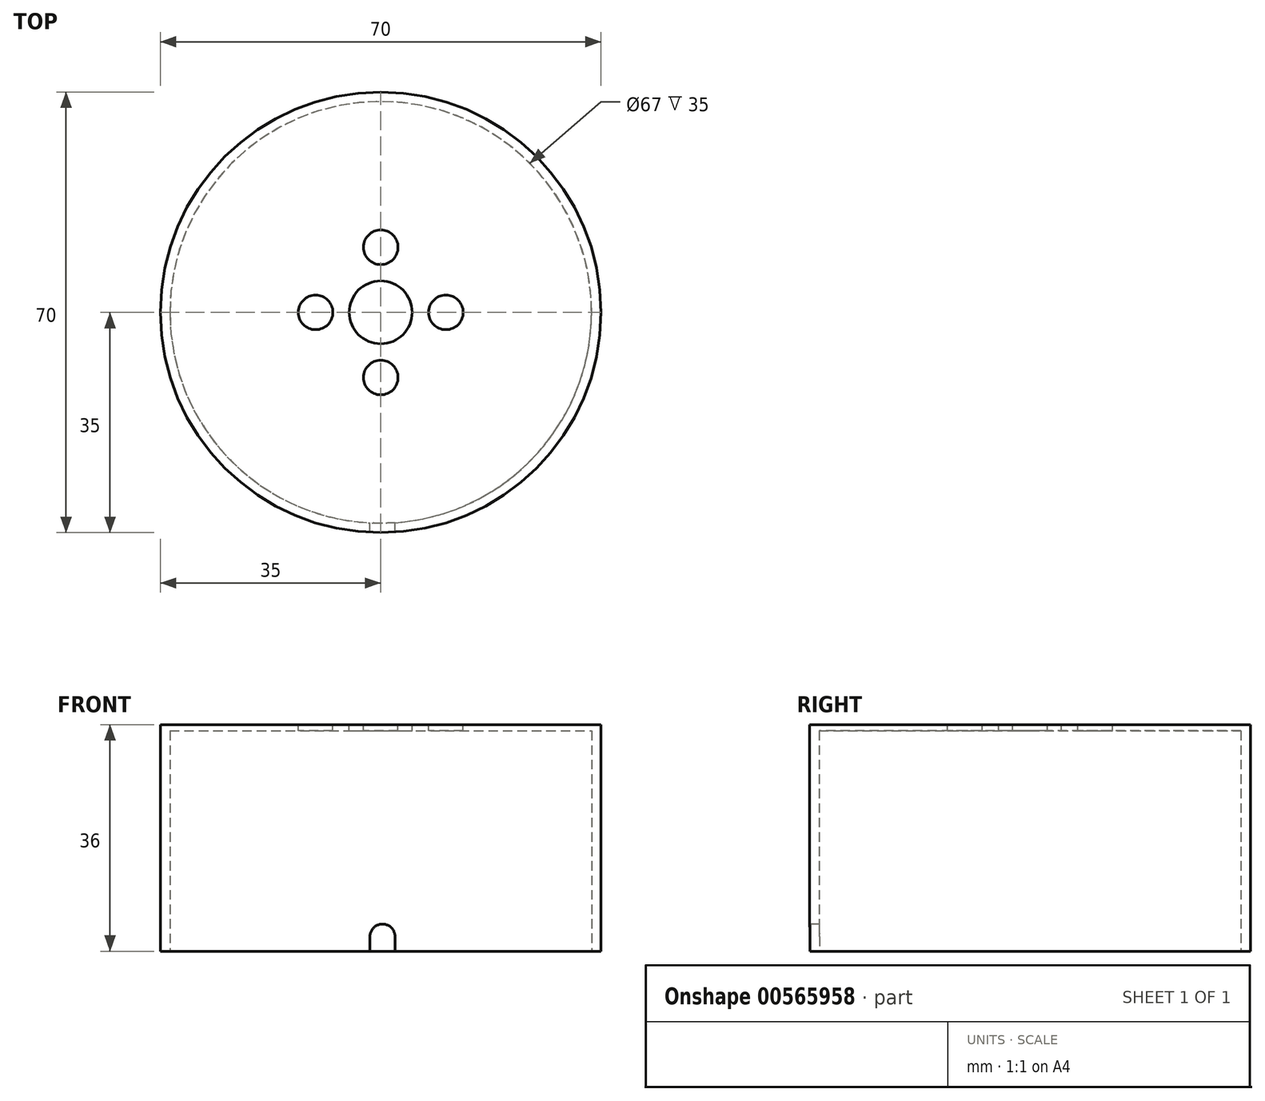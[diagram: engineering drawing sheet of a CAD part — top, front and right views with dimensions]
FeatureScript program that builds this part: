
annotation { "Feature Type Name" : "Feature", "Feature Type Description" : "" }
export const myFeature = defineFeature(function(context is Context, id is Id, definition is map)
    precondition{}
    {
        {
            var Q0;
            Q0=qCreatedBy(makeId("Top.planeOp"),FACE);
            var sketch = newSketch(context, id + "F0", { "sketchPlane" : qUnion([Q0])});
            skCircle(sketch, "E0", {"center": v(0, 0) * mm, "radius": 5 * mm});
            skCircle(sketch, "E1", {"center": v(0, 0) * mm, "radius": 5.5 * mm});
            skLineSegment(sketch, "E2", {"start": v(-0.75, 5.45) * mm, "end": v(-0.75, 25.45) * mm});
            skLineSegment(sketch, "E3", {"start": v(0.75, 5.45) * mm, "end": v(0.75, 25.45) * mm});
            skLineSegment(sketch, "E4", {"start": v(-0.75, 10.35) * mm, "end": v(0.75, 10.35) * mm, "construction": true});
            skCircle(sketch, "E5", {"center": v(0, 10.35) * mm, "radius": 2.75 * mm});
            skLineSegment(sketch, "E6", {"start": v(-0.75, 25.45) * mm, "end": v(0.75, 25.45) * mm});
            skCircle(sketch, "E7.MirrorC", {"center": v(-10.35, 0) * mm, "radius": 2.75 * mm});
            skLineSegment(sketch, "E8.MirrorCS", {"start": v(-5.45, 0.75) * mm, "end": v(-25.45, 0.75) * mm});
            skLineSegment(sketch, "E9.MirrorCS", {"start": v(-5.45, -0.75) * mm, "end": v(-25.45, -0.75) * mm});
            skLineSegment(sketch, "E10.MirrorCS", {"start": v(-25.45, 0.75) * mm, "end": v(-25.45, -0.75) * mm});
            skLineSegment(sketch, "E11.MirrorCS", {"start": v(-0.75, -5.45) * mm, "end": v(-0.75, -25.45) * mm});
            skLineSegment(sketch, "E12.MirrorCS", {"start": v(0.75, -25.45) * mm, "end": v(-0.75, -25.45) * mm});
            skLineSegment(sketch, "E13.MirrorCS", {"start": v(0.75, -5.45) * mm, "end": v(0.75, -25.45) * mm});
            skCircle(sketch, "E14.MirrorC", {"center": v(0, -10.35) * mm, "radius": 2.75 * mm});
            skLineSegment(sketch, "E15.MirrorCS", {"start": v(5.45, -0.75) * mm, "end": v(25.45, -0.75) * mm});
            skLineSegment(sketch, "E16.MirrorCS", {"start": v(25.45, 0.75) * mm, "end": v(25.45, -0.75) * mm});
            skLineSegment(sketch, "E17.MirrorCS", {"start": v(5.45, 0.75) * mm, "end": v(25.45, 0.75) * mm});
            skCircle(sketch, "E18.MirrorC", {"center": v(10.35, 0) * mm, "radius": 2.75 * mm});
            skCircle(sketch, "E19", {"center": v(0, 0) * mm, "radius": 35 * mm});
            skSolve(sketch);
        }
        {
            var Q0;
            Q0 = qSketchRegion(id + "F0", true);
            var Q1;
            {var subQ16=sQuery(id+"F0.wireOp",EDGE,"E6");Q1=makeQuery(id+"F0.imprint","IMPRINT",FACE,{"disambiguationData":[TD([[makeQuery(id+"F0.imprint","IMPRINT",EDGE,{"derivedFrom":subQ16}),1.0]])]});}
            var Q2;
            {var subQ0=sQuery(id+"F0.wireOp",EDGE,"E14.MirrorC");var subQ1=sQuery(id+"F0.wireOp",EDGE,"E11.MirrorCS");var subQ2=makeQuery(id+"F0.imprint","INTERSECT",VERTEX,{"disambiguationData":[OD(0.0)],"derivedFrom":[subQ1,subQ0]});Q2=makeQuery(id+"F0.imprint","IMPRINT",FACE,{"disambiguationData":[TD([[makeQuery(id+"F0.imprint","IMPRINT",EDGE,{"disambiguationData":[TD([[subQ2,-1.0]])],"derivedFrom":subQ1}),1.0]])]});}
            var Q3;
            {var subQ0=sQuery(id+"F0.wireOp",EDGE,"E18.MirrorC");var subQ1=sQuery(id+"F0.wireOp",EDGE,"E15.MirrorCS");var subQ2=makeQuery(id+"F0.imprint","INTERSECT",VERTEX,{"disambiguationData":[OD(0.0)],"derivedFrom":[subQ1,subQ0]});Q3=makeQuery(id+"F0.imprint","IMPRINT",FACE,{"disambiguationData":[TD([[makeQuery(id+"F0.imprint","IMPRINT",EDGE,{"disambiguationData":[TD([[subQ2,-1.0]])],"derivedFrom":subQ1}),1.0]])]});}
            var Q4;
            {var subQ0=sQuery(id+"F0.wireOp",EDGE,"E8.MirrorCS");var subQ1=sQuery(id+"F0.wireOp",EDGE,"E1");var subQ2=makeQuery(id+"F0.imprint","INTERSECT",VERTEX,{"derivedFrom":[subQ1,subQ0]});Q4=makeQuery(id+"F0.imprint","IMPRINT",FACE,{"disambiguationData":[TD([[makeQuery(id+"F0.imprint","IMPRINT",EDGE,{"disambiguationData":[TD([[subQ2,-1.0]])],"derivedFrom":subQ1}),-1.0]])]});}
            var Q5;
            {var subQ0=sQuery(id+"F0.wireOp",EDGE,"E8.MirrorCS");var subQ1=sQuery(id+"F0.wireOp",EDGE,"E7.MirrorC");var subQ2=makeQuery(id+"F0.imprint","INTERSECT",VERTEX,{"disambiguationData":[OD(0.0)],"derivedFrom":[subQ1,subQ0]});Q5=makeQuery(id+"F0.imprint","IMPRINT",FACE,{"disambiguationData":[TD([[makeQuery(id+"F0.imprint","IMPRINT",EDGE,{"disambiguationData":[TD([[subQ2,-1.0]])],"derivedFrom":subQ1}),-1.0]])]});}
            var Q6;
            {var subQ0=sQuery(id+"F0.wireOp",EDGE,"E6");Q6=makeQuery(id+"F0.imprint","IMPRINT",FACE,{"disambiguationData":[TD([[makeQuery(id+"F0.imprint","IMPRINT",EDGE,{"derivedFrom":subQ0}),-1.0]])]});}
            var Q7;
            {var subQ0=sQuery(id+"F0.wireOp",EDGE,"E9.MirrorCS");var subQ1=sQuery(id+"F0.wireOp",EDGE,"E7.MirrorC");var subQ2=makeQuery(id+"F0.imprint","INTERSECT",VERTEX,{"disambiguationData":[OD(0.0)],"derivedFrom":[subQ1,subQ0]});Q7=makeQuery(id+"F0.imprint","IMPRINT",FACE,{"disambiguationData":[TD([[makeQuery(id+"F0.imprint","IMPRINT",EDGE,{"disambiguationData":[TD([[subQ2,-1.0]])],"derivedFrom":subQ1}),-1.0]])]});}
            var Q8;
            {var subQ5=sQuery(id+"F0.wireOp",EDGE,"E10.MirrorCS");Q8=makeQuery(id+"F0.imprint","IMPRINT",FACE,{"disambiguationData":[TD([[makeQuery(id+"F0.imprint","IMPRINT",EDGE,{"derivedFrom":subQ5}),1.0]])]});}
            var Q9;
            {var subQ0=sQuery(id+"F0.wireOp",EDGE,"E14.MirrorC");var subQ1=sQuery(id+"F0.wireOp",EDGE,"E11.MirrorCS");var subQ2=makeQuery(id+"F0.imprint","INTERSECT",VERTEX,{"disambiguationData":[OD(0.0)],"derivedFrom":[subQ1,subQ0]});Q9=makeQuery(id+"F0.imprint","IMPRINT",FACE,{"disambiguationData":[TD([[makeQuery(id+"F0.imprint","IMPRINT",EDGE,{"disambiguationData":[TD([[subQ2,-1.0]])],"derivedFrom":subQ1}),-1.0]])]});}
            var Q10;
            {var subQ0=sQuery(id+"F0.wireOp",EDGE,"E12.MirrorCS");Q10=makeQuery(id+"F0.imprint","IMPRINT",FACE,{"disambiguationData":[TD([[makeQuery(id+"F0.imprint","IMPRINT",EDGE,{"derivedFrom":subQ0}),-1.0]])]});}
            var Q11;
            {var subQ0=sQuery(id+"F0.wireOp",EDGE,"E14.MirrorC");var subQ1=sQuery(id+"F0.wireOp",EDGE,"E13.MirrorCS");var subQ2=makeQuery(id+"F0.imprint","INTERSECT",VERTEX,{"disambiguationData":[OD(0.0)],"derivedFrom":[subQ1,subQ0]});Q11=makeQuery(id+"F0.imprint","IMPRINT",FACE,{"disambiguationData":[TD([[makeQuery(id+"F0.imprint","IMPRINT",EDGE,{"disambiguationData":[TD([[subQ2,-1.0]])],"derivedFrom":subQ1}),1.0]])]});}
            var Q12;
            {var subQ0=sQuery(id+"F0.wireOp",EDGE,"E18.MirrorC");var subQ1=sQuery(id+"F0.wireOp",EDGE,"E15.MirrorCS");var subQ2=makeQuery(id+"F0.imprint","INTERSECT",VERTEX,{"disambiguationData":[OD(0.0)],"derivedFrom":[subQ1,subQ0]});Q12=makeQuery(id+"F0.imprint","IMPRINT",FACE,{"disambiguationData":[TD([[makeQuery(id+"F0.imprint","IMPRINT",EDGE,{"disambiguationData":[TD([[subQ2,-1.0]])],"derivedFrom":subQ1}),-1.0]])]});}
            var Q13;
            {var subQ0=sQuery(id+"F0.wireOp",EDGE,"E16.MirrorCS");Q13=makeQuery(id+"F0.imprint","IMPRINT",FACE,{"disambiguationData":[TD([[makeQuery(id+"F0.imprint","IMPRINT",EDGE,{"derivedFrom":subQ0}),-1.0]])]});}
            var Q14;
            Q14=makeQuery(id+"F0.imprint","IMPRINT",FACE,{"disambiguationData":[TD([[makeQuery(id+"F0.imprint","IMPRINT",EDGE,{"derivedFrom":sQuery(id+"F0.wireOp",EDGE,"E0")}),-1.0]])]});
            var Q15;
            {var subQ0=sQuery(id+"F0.wireOp",EDGE,"E18.MirrorC");var subQ1=sQuery(id+"F0.wireOp",EDGE,"E17.MirrorCS");var subQ2=makeQuery(id+"F0.imprint","INTERSECT",VERTEX,{"disambiguationData":[OD(0.0)],"derivedFrom":[subQ1,subQ0]});Q15=makeQuery(id+"F0.imprint","IMPRINT",FACE,{"disambiguationData":[TD([[makeQuery(id+"F0.imprint","IMPRINT",EDGE,{"disambiguationData":[TD([[subQ2,-1.0]])],"derivedFrom":subQ1}),1.0]])]});}
            var Q16;
            {var subQ0=sQuery(id+"F0.wireOp",EDGE,"E5");var subQ1=sQuery(id+"F0.wireOp",EDGE,"E2");var subQ2=makeQuery(id+"F0.imprint","INTERSECT",VERTEX,{"disambiguationData":[OD(0.0)],"derivedFrom":[subQ1,subQ0]});Q16=makeQuery(id+"F0.imprint","IMPRINT",FACE,{"disambiguationData":[TD([[makeQuery(id+"F0.imprint","IMPRINT",EDGE,{"disambiguationData":[TD([[subQ2,-1.0]])],"derivedFrom":subQ1}),-1.0]])]});}
            var Q17;
            {var subQ0=sQuery(id+"F0.wireOp",EDGE,"E15.MirrorCS");var subQ1=sQuery(id+"F0.wireOp",EDGE,"E1");var subQ2=makeQuery(id+"F0.imprint","INTERSECT",VERTEX,{"derivedFrom":[subQ1,subQ0]});Q17=makeQuery(id+"F0.imprint","IMPRINT",FACE,{"disambiguationData":[TD([[makeQuery(id+"F0.imprint","IMPRINT",EDGE,{"disambiguationData":[TD([[subQ2,-1.0]])],"derivedFrom":subQ1}),-1.0]])]});}
            var Q18;
            {var subQ0=sQuery(id+"F0.wireOp",EDGE,"E11.MirrorCS");var subQ1=sQuery(id+"F0.wireOp",EDGE,"E1");var subQ2=makeQuery(id+"F0.imprint","INTERSECT",VERTEX,{"derivedFrom":[subQ1,subQ0]});Q18=makeQuery(id+"F0.imprint","IMPRINT",FACE,{"disambiguationData":[TD([[makeQuery(id+"F0.imprint","IMPRINT",EDGE,{"disambiguationData":[TD([[subQ2,-1.0]])],"derivedFrom":subQ1}),-1.0]])]});}
            var Q19;
            {var subQ0=sQuery(id+"F0.wireOp",EDGE,"E2");var subQ1=sQuery(id+"F0.wireOp",EDGE,"E1");var subQ2=makeQuery(id+"F0.imprint","INTERSECT",VERTEX,{"derivedFrom":[subQ1,subQ0]});Q19=makeQuery(id+"F0.imprint","IMPRINT",FACE,{"disambiguationData":[TD([[makeQuery(id+"F0.imprint","IMPRINT",EDGE,{"disambiguationData":[TD([[subQ2,1.0]])],"derivedFrom":subQ1}),-1.0]])]});}
            var Q20;
            Q20=makeQuery(id+"F0.imprint","IMPRINT",FACE,{"disambiguationData":[TD([[makeQuery(id+"F0.imprint","IMPRINT",EDGE,{"derivedFrom":sQuery(id+"F0.wireOp",EDGE,"E0")}),1.0]])]});
            var Q21;
            {var subQ0=sQuery(id+"F0.wireOp",EDGE,"E5");var subQ1=sQuery(id+"F0.wireOp",EDGE,"E2");var subQ2=makeQuery(id+"F0.imprint","INTERSECT",VERTEX,{"disambiguationData":[OD(0.0)],"derivedFrom":[subQ1,subQ0]});Q21=makeQuery(id+"F0.imprint","IMPRINT",FACE,{"disambiguationData":[TD([[makeQuery(id+"F0.imprint","IMPRINT",EDGE,{"disambiguationData":[TD([[subQ2,-1.0]])],"derivedFrom":subQ1}),1.0]])]});}
            var Q22;
            {var subQ0=sQuery(id+"F0.wireOp",EDGE,"E5");var subQ1=sQuery(id+"F0.wireOp",EDGE,"E3");var subQ2=makeQuery(id+"F0.imprint","INTERSECT",VERTEX,{"disambiguationData":[OD(0.0)],"derivedFrom":[subQ1,subQ0]});Q22=makeQuery(id+"F0.imprint","IMPRINT",FACE,{"disambiguationData":[TD([[makeQuery(id+"F0.imprint","IMPRINT",EDGE,{"disambiguationData":[TD([[subQ2,-1.0]])],"derivedFrom":subQ1}),-1.0]])]});}
            var Q23;
            {var subQ0=sQuery(id+"F0.wireOp",EDGE,"E8.MirrorCS");var subQ1=sQuery(id+"F0.wireOp",EDGE,"E7.MirrorC");var subQ2=makeQuery(id+"F0.imprint","INTERSECT",VERTEX,{"disambiguationData":[OD(0.0)],"derivedFrom":[subQ1,subQ0]});Q23=makeQuery(id+"F0.imprint","IMPRINT",FACE,{"disambiguationData":[TD([[makeQuery(id+"F0.imprint","IMPRINT",EDGE,{"disambiguationData":[TD([[subQ2,1.0]])],"derivedFrom":subQ1}),-1.0]])]});}
            extrude(context, id + "F1", {"entities" : qUnion([Q0, Q1, Q2, Q3, Q4, Q5, Q6, Q7, Q8, Q9, Q10, Q11, Q12, Q13, Q14, Q15, Q16, Q17, Q18, Q19, Q20, Q21, Q22, Q23]), "oppositeDirection" : true, "depth" : 38 * mm, "offsetDistance" : 25 * mm});
        }
        {
            var Q0;
            {var subQ0=sQuery(id+"F0.wireOp",EDGE,"E9.MirrorCS");var subQ1=sQuery(id+"F0.wireOp",EDGE,"E7.MirrorC");var subQ2=makeQuery(id+"F0.imprint","INTERSECT",VERTEX,{"disambiguationData":[OD(0.0)],"derivedFrom":[subQ1,subQ0]});Q0=makeQuery(id+"F0.imprint","IMPRINT",FACE,{"disambiguationData":[TD([[makeQuery(id+"F0.imprint","IMPRINT",EDGE,{"disambiguationData":[TD([[subQ2,-1.0]])],"derivedFrom":subQ1}),-1.0]])]});}
            var Q1;
            {var subQ0=sQuery(id+"F0.wireOp",EDGE,"E8.MirrorCS");var subQ1=sQuery(id+"F0.wireOp",EDGE,"E7.MirrorC");var subQ2=makeQuery(id+"F0.imprint","INTERSECT",VERTEX,{"disambiguationData":[OD(0.0)],"derivedFrom":[subQ1,subQ0]});Q1=makeQuery(id+"F0.imprint","IMPRINT",FACE,{"disambiguationData":[TD([[makeQuery(id+"F0.imprint","IMPRINT",EDGE,{"disambiguationData":[TD([[subQ2,-1.0]])],"derivedFrom":subQ1}),-1.0]])]});}
            var Q2;
            {var subQ0=sQuery(id+"F0.wireOp",EDGE,"E8.MirrorCS");var subQ1=sQuery(id+"F0.wireOp",EDGE,"E7.MirrorC");var subQ2=makeQuery(id+"F0.imprint","INTERSECT",VERTEX,{"disambiguationData":[OD(0.0)],"derivedFrom":[subQ1,subQ0]});Q2=makeQuery(id+"F0.imprint","IMPRINT",FACE,{"disambiguationData":[TD([[makeQuery(id+"F0.imprint","IMPRINT",EDGE,{"disambiguationData":[TD([[subQ2,1.0]])],"derivedFrom":subQ1}),-1.0]])]});}
            var Q3;
            {var subQ5=sQuery(id+"F0.wireOp",EDGE,"E10.MirrorCS");Q3=makeQuery(id+"F0.imprint","IMPRINT",FACE,{"disambiguationData":[TD([[makeQuery(id+"F0.imprint","IMPRINT",EDGE,{"derivedFrom":subQ5}),1.0]])]});}
            var Q4;
            {var subQ0=sQuery(id+"F0.wireOp",EDGE,"E8.MirrorCS");var subQ1=sQuery(id+"F0.wireOp",EDGE,"E1");var subQ2=makeQuery(id+"F0.imprint","INTERSECT",VERTEX,{"derivedFrom":[subQ1,subQ0]});Q4=makeQuery(id+"F0.imprint","IMPRINT",FACE,{"disambiguationData":[TD([[makeQuery(id+"F0.imprint","IMPRINT",EDGE,{"disambiguationData":[TD([[subQ2,-1.0]])],"derivedFrom":subQ1}),-1.0]])]});}
            var Q5;
            Q5=makeQuery(id+"F0.imprint","IMPRINT",FACE,{"disambiguationData":[TD([[makeQuery(id+"F0.imprint","IMPRINT",EDGE,{"derivedFrom":sQuery(id+"F0.wireOp",EDGE,"E0")}),-1.0]])]});
            var Q6;
            {var subQ0=sQuery(id+"F0.wireOp",EDGE,"E5");var subQ1=sQuery(id+"F0.wireOp",EDGE,"E3");var subQ2=makeQuery(id+"F0.imprint","INTERSECT",VERTEX,{"disambiguationData":[OD(0.0)],"derivedFrom":[subQ1,subQ0]});Q6=makeQuery(id+"F0.imprint","IMPRINT",FACE,{"disambiguationData":[TD([[makeQuery(id+"F0.imprint","IMPRINT",EDGE,{"disambiguationData":[TD([[subQ2,-1.0]])],"derivedFrom":subQ1}),-1.0]])]});}
            var Q7;
            {var subQ0=sQuery(id+"F0.wireOp",EDGE,"E5");var subQ1=sQuery(id+"F0.wireOp",EDGE,"E2");var subQ2=makeQuery(id+"F0.imprint","INTERSECT",VERTEX,{"disambiguationData":[OD(0.0)],"derivedFrom":[subQ1,subQ0]});Q7=makeQuery(id+"F0.imprint","IMPRINT",FACE,{"disambiguationData":[TD([[makeQuery(id+"F0.imprint","IMPRINT",EDGE,{"disambiguationData":[TD([[subQ2,-1.0]])],"derivedFrom":subQ1}),1.0]])]});}
            var Q8;
            {var subQ0=sQuery(id+"F0.wireOp",EDGE,"E5");var subQ1=sQuery(id+"F0.wireOp",EDGE,"E2");var subQ2=makeQuery(id+"F0.imprint","INTERSECT",VERTEX,{"disambiguationData":[OD(0.0)],"derivedFrom":[subQ1,subQ0]});Q8=makeQuery(id+"F0.imprint","IMPRINT",FACE,{"disambiguationData":[TD([[makeQuery(id+"F0.imprint","IMPRINT",EDGE,{"disambiguationData":[TD([[subQ2,-1.0]])],"derivedFrom":subQ1}),-1.0]])]});}
            var Q9;
            {var subQ0=sQuery(id+"F0.wireOp",EDGE,"E2");var subQ1=sQuery(id+"F0.wireOp",EDGE,"E1");var subQ2=makeQuery(id+"F0.imprint","INTERSECT",VERTEX,{"derivedFrom":[subQ1,subQ0]});Q9=makeQuery(id+"F0.imprint","IMPRINT",FACE,{"disambiguationData":[TD([[makeQuery(id+"F0.imprint","IMPRINT",EDGE,{"disambiguationData":[TD([[subQ2,1.0]])],"derivedFrom":subQ1}),-1.0]])]});}
            var Q10;
            {var subQ0=sQuery(id+"F0.wireOp",EDGE,"E6");Q10=makeQuery(id+"F0.imprint","IMPRINT",FACE,{"disambiguationData":[TD([[makeQuery(id+"F0.imprint","IMPRINT",EDGE,{"derivedFrom":subQ0}),-1.0]])]});}
            var Q11;
            {var subQ0=sQuery(id+"F0.wireOp",EDGE,"E18.MirrorC");var subQ1=sQuery(id+"F0.wireOp",EDGE,"E15.MirrorCS");var subQ2=makeQuery(id+"F0.imprint","INTERSECT",VERTEX,{"disambiguationData":[OD(0.0)],"derivedFrom":[subQ1,subQ0]});Q11=makeQuery(id+"F0.imprint","IMPRINT",FACE,{"disambiguationData":[TD([[makeQuery(id+"F0.imprint","IMPRINT",EDGE,{"disambiguationData":[TD([[subQ2,-1.0]])],"derivedFrom":subQ1}),1.0]])]});}
            var Q12;
            {var subQ0=sQuery(id+"F0.wireOp",EDGE,"E18.MirrorC");var subQ1=sQuery(id+"F0.wireOp",EDGE,"E17.MirrorCS");var subQ2=makeQuery(id+"F0.imprint","INTERSECT",VERTEX,{"disambiguationData":[OD(0.0)],"derivedFrom":[subQ1,subQ0]});Q12=makeQuery(id+"F0.imprint","IMPRINT",FACE,{"disambiguationData":[TD([[makeQuery(id+"F0.imprint","IMPRINT",EDGE,{"disambiguationData":[TD([[subQ2,-1.0]])],"derivedFrom":subQ1}),1.0]])]});}
            var Q13;
            {var subQ0=sQuery(id+"F0.wireOp",EDGE,"E18.MirrorC");var subQ1=sQuery(id+"F0.wireOp",EDGE,"E15.MirrorCS");var subQ2=makeQuery(id+"F0.imprint","INTERSECT",VERTEX,{"disambiguationData":[OD(0.0)],"derivedFrom":[subQ1,subQ0]});Q13=makeQuery(id+"F0.imprint","IMPRINT",FACE,{"disambiguationData":[TD([[makeQuery(id+"F0.imprint","IMPRINT",EDGE,{"disambiguationData":[TD([[subQ2,-1.0]])],"derivedFrom":subQ1}),-1.0]])]});}
            var Q14;
            {var subQ0=sQuery(id+"F0.wireOp",EDGE,"E15.MirrorCS");var subQ1=sQuery(id+"F0.wireOp",EDGE,"E1");var subQ2=makeQuery(id+"F0.imprint","INTERSECT",VERTEX,{"derivedFrom":[subQ1,subQ0]});Q14=makeQuery(id+"F0.imprint","IMPRINT",FACE,{"disambiguationData":[TD([[makeQuery(id+"F0.imprint","IMPRINT",EDGE,{"disambiguationData":[TD([[subQ2,-1.0]])],"derivedFrom":subQ1}),-1.0]])]});}
            var Q15;
            {var subQ0=sQuery(id+"F0.wireOp",EDGE,"E16.MirrorCS");Q15=makeQuery(id+"F0.imprint","IMPRINT",FACE,{"disambiguationData":[TD([[makeQuery(id+"F0.imprint","IMPRINT",EDGE,{"derivedFrom":subQ0}),-1.0]])]});}
            var Q16;
            {var subQ0=sQuery(id+"F0.wireOp",EDGE,"E12.MirrorCS");Q16=makeQuery(id+"F0.imprint","IMPRINT",FACE,{"disambiguationData":[TD([[makeQuery(id+"F0.imprint","IMPRINT",EDGE,{"derivedFrom":subQ0}),-1.0]])]});}
            var Q17;
            {var subQ0=sQuery(id+"F0.wireOp",EDGE,"E14.MirrorC");var subQ1=sQuery(id+"F0.wireOp",EDGE,"E11.MirrorCS");var subQ2=makeQuery(id+"F0.imprint","INTERSECT",VERTEX,{"disambiguationData":[OD(0.0)],"derivedFrom":[subQ1,subQ0]});Q17=makeQuery(id+"F0.imprint","IMPRINT",FACE,{"disambiguationData":[TD([[makeQuery(id+"F0.imprint","IMPRINT",EDGE,{"disambiguationData":[TD([[subQ2,-1.0]])],"derivedFrom":subQ1}),1.0]])]});}
            var Q18;
            {var subQ0=sQuery(id+"F0.wireOp",EDGE,"E14.MirrorC");var subQ1=sQuery(id+"F0.wireOp",EDGE,"E11.MirrorCS");var subQ2=makeQuery(id+"F0.imprint","INTERSECT",VERTEX,{"disambiguationData":[OD(0.0)],"derivedFrom":[subQ1,subQ0]});Q18=makeQuery(id+"F0.imprint","IMPRINT",FACE,{"disambiguationData":[TD([[makeQuery(id+"F0.imprint","IMPRINT",EDGE,{"disambiguationData":[TD([[subQ2,-1.0]])],"derivedFrom":subQ1}),-1.0]])]});}
            var Q19;
            {var subQ0=sQuery(id+"F0.wireOp",EDGE,"E14.MirrorC");var subQ1=sQuery(id+"F0.wireOp",EDGE,"E13.MirrorCS");var subQ2=makeQuery(id+"F0.imprint","INTERSECT",VERTEX,{"disambiguationData":[OD(0.0)],"derivedFrom":[subQ1,subQ0]});Q19=makeQuery(id+"F0.imprint","IMPRINT",FACE,{"disambiguationData":[TD([[makeQuery(id+"F0.imprint","IMPRINT",EDGE,{"disambiguationData":[TD([[subQ2,-1.0]])],"derivedFrom":subQ1}),1.0]])]});}
            var Q20;
            {var subQ0=sQuery(id+"F0.wireOp",EDGE,"E11.MirrorCS");var subQ1=sQuery(id+"F0.wireOp",EDGE,"E1");var subQ2=makeQuery(id+"F0.imprint","INTERSECT",VERTEX,{"derivedFrom":[subQ1,subQ0]});Q20=makeQuery(id+"F0.imprint","IMPRINT",FACE,{"disambiguationData":[TD([[makeQuery(id+"F0.imprint","IMPRINT",EDGE,{"disambiguationData":[TD([[subQ2,-1.0]])],"derivedFrom":subQ1}),-1.0]])]});}
            extrude(context, id + "F2", {"entities" : qUnion([Q0, Q1, Q2, Q3, Q4, Q5, Q6, Q7, Q8, Q9, Q10, Q11, Q12, Q13, Q14, Q15, Q16, Q17, Q18, Q19, Q20]), "operationType" : NewBodyOperationType.REMOVE, "oppositeDirection" : true, "depth" : 2 * mm, "offsetDistance" : 25 * mm});
        }
        {
            var Q0;
            Q0=makeQuery(id+"F1.opExtrude","CAP_FACE",FACE,{"disambiguationData":[OSD([sQuery(id+"F0.wireOp",EDGE,"E19")])],"isStart":false});
            var sketch = newSketch(context, id + "F3", { "sketchPlane" : qUnion([Q0])});
            skCircle(sketch, "E20", {"center": v(0, 0) * mm, "radius": 33.5 * mm});
            skSolve(sketch);
        }
        {
            var Q0;
            Q0=makeQuery(id+"F3.imprint","IMPRINT",FACE,{"disambiguationData":[TD([[makeQuery(id+"F3.imprint","IMPRINT",EDGE,{"derivedFrom":sQuery(id+"F3.wireOp",EDGE,"E20")}),1.0]])]});
            extrude(context, id + "F4", {"entities" : qUnion([Q0]), "operationType" : NewBodyOperationType.REMOVE, "oppositeDirection" : true, "depth" : 35 * mm, "offsetDistance" : 25 * mm});
        }
        {
            var Q0;
            Q0=makeQuery(id+"F0.imprint","IMPRINT",FACE,{"disambiguationData":[TD([[makeQuery(id+"F0.imprint","IMPRINT",EDGE,{"derivedFrom":sQuery(id+"F0.wireOp",EDGE,"E0")}),1.0]])]});
            var Q1;
            Q1=makeQuery(id+"F4.boolean.opBoolean","COPY",FACE,{"derivedFrom":makeQuery(id+"F4.opExtrude","CAP_FACE",FACE,{"disambiguationData":[OSD([sQuery(id+"F3.wireOp",EDGE,"E20")])],"isStart":false})});
            extrude(context, id + "F5", {"entities" : qUnion([Q0]), "operationType" : NewBodyOperationType.REMOVE, "endBound" : BoundingType.THROUGH_ALL, "oppositeDirection" : true, "depth" : 3 * mm, "endBoundEntityFace" : qUnion([Q1]), "offsetDistance" : 25 * mm});
        }
        {
            var Q0;
            Q0=qCreatedBy(makeId("Front.planeOp"),FACE);
            cPlane(context, id + "F6", {"entities" : qUnion([Q0]), "cplaneType" : CPlaneType.OFFSET, "offset" : 35 * mm, "width" : 150 * mm, "height" : 150 * mm});
        }
        {
            var Q0;
            Q0=qCreatedBy(id+"F6.planeOp",FACE);
            var sketch = newSketch(context, id + "F7", { "sketchPlane" : qUnion([Q0])});
            skLineSegment(sketch, "E21.bottom", {"start": v(-1.72, -38.19) * mm, "end": v(2.28, -38.19) * mm});
            skLineSegment(sketch, "E21.top", {"start": v(-1.72, -33.69) * mm, "end": v(2.28, -33.69) * mm});
            skLineSegment(sketch, "E21.left", {"start": v(-1.72, -38.19) * mm, "end": v(-1.72, -33.69) * mm});
            skLineSegment(sketch, "E21.right", {"start": v(2.28, -38.19) * mm, "end": v(2.28, -33.69) * mm});
            skSolve(sketch);
        }
        {
            var Q0;
            Q0=makeQuery(id+"F7.imprint","IMPRINT",FACE,{"disambiguationData":[TD([[makeQuery(id+"F7.imprint","IMPRINT",EDGE,{"derivedFrom":sQuery(id+"F7.wireOp",EDGE,"E21.bottom")}),1.0]])]});
            extrude(context, id + "F8", {"entities" : qUnion([Q0]), "operationType" : NewBodyOperationType.REMOVE, "oppositeDirection" : true, "depth" : 2 * mm, "offsetDistance" : 25 * mm});
        }
        {
            var Q0;
            Q0=makeQuery(id+"F8.boolean.opBoolean","COPY",EDGE,{"derivedFrom":makeQuery(id+"F8.opExtrude","SWEPT_EDGE",EDGE,{"disambiguationData":[OSD([sQuery(id+"F7.wireOp",EDGE,"E21.top"),sQuery(id+"F7.wireOp",EDGE,"E21.right")])]})});
            var Q1;
            Q1=makeQuery(id+"F8.boolean.opBoolean","COPY",EDGE,{"derivedFrom":makeQuery(id+"F8.opExtrude","SWEPT_EDGE",EDGE,{"disambiguationData":[OSD([sQuery(id+"F7.wireOp",EDGE,"E21.top"),sQuery(id+"F7.wireOp",EDGE,"E21.left")])]})});
            fillet(context, id + "F9", {"entities" : qUnion([Q0, Q1]), "radius" : 2 * mm, "tangentPropagation" : true, "allowEdgeOverflow" : false});
        }
    });
